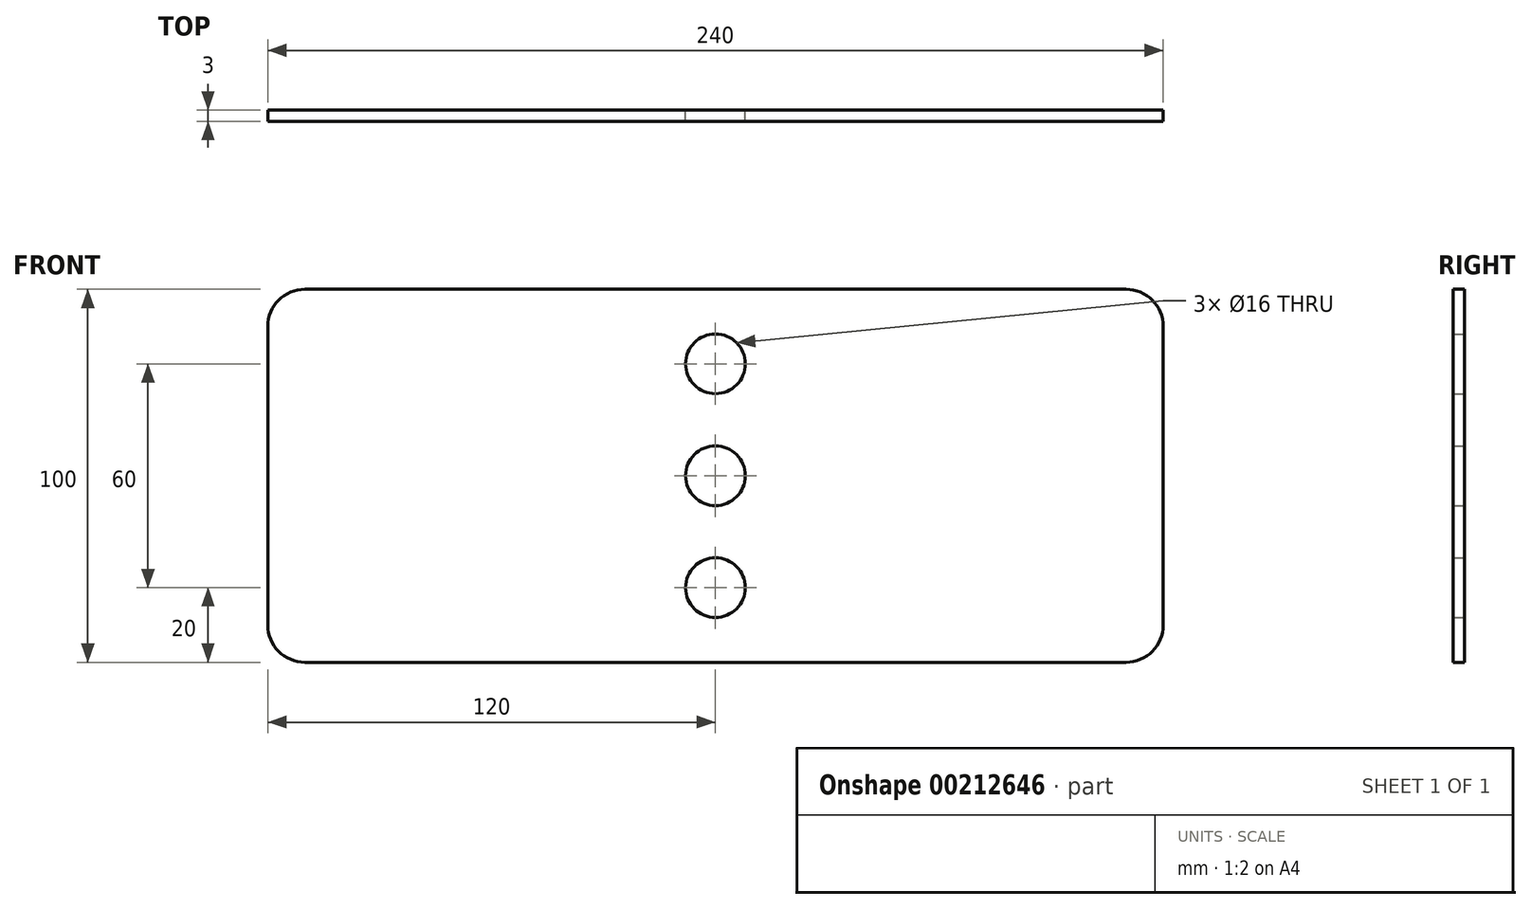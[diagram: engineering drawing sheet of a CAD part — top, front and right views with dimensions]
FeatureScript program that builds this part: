
annotation { "Feature Type Name" : "Feature", "Feature Type Description" : "" }
export const myFeature = defineFeature(function(context is Context, id is Id, definition is map)
    precondition{}
    {
        {
            var Q0;
            Q0=qCreatedBy(makeId("Front.planeOp"),FACE);
            var sketch = newSketch(context, id + "F0", { "sketchPlane" : qUnion([Q0])});
            skLineSegment(sketch, "E0.bottom", {"start": v(-120, 50) * mm, "end": v(120, 50) * mm});
            skLineSegment(sketch, "E0.top", {"start": v(-120, -50) * mm, "end": v(120, -50) * mm});
            skLineSegment(sketch, "E0.left", {"start": v(-120, 50) * mm, "end": v(-120, -50) * mm});
            skLineSegment(sketch, "E0.right", {"start": v(120, 50) * mm, "end": v(120, -50) * mm});
            skCircle(sketch, "E1", {"center": v(0, 0) * mm, "radius": 8 * mm});
            skCircle(sketch, "E2", {"center": v(0, 30) * mm, "radius": 8 * mm});
            skCircle(sketch, "E3", {"center": v(0, -30) * mm, "radius": 8 * mm});
            skSolve(sketch);
        }
        {
            var Q0;
            Q0 = qSketchRegion(id + "F0", true);
            extrude(context, id + "F1", {"entities" : qUnion([Q0]), "depth" : 3 * mm});
        }
        {
            var Q0;
            Q0=makeQuery(id+"F1.opExtrude","SWEPT_EDGE",EDGE,{"disambiguationData":[OSD([sQuery(id+"F0.wireOp",EDGE,"E0.bottom"),sQuery(id+"F0.wireOp",EDGE,"E0.left")])]});
            var Q1;
            Q1=makeQuery(id+"F1.opExtrude","SWEPT_EDGE",EDGE,{"disambiguationData":[OSD([sQuery(id+"F0.wireOp",EDGE,"E0.top"),sQuery(id+"F0.wireOp",EDGE,"E0.left")])]});
            var Q2;
            Q2=makeQuery(id+"F1.opExtrude","SWEPT_EDGE",EDGE,{"disambiguationData":[OSD([sQuery(id+"F0.wireOp",EDGE,"E0.bottom"),sQuery(id+"F0.wireOp",EDGE,"E0.right")])]});
            var Q3;
            Q3=makeQuery(id+"F1.opExtrude","SWEPT_EDGE",EDGE,{"disambiguationData":[OSD([sQuery(id+"F0.wireOp",EDGE,"E0.top"),sQuery(id+"F0.wireOp",EDGE,"E0.right")])]});
            fillet(context, id + "F2", {"entities" : qUnion([Q0, Q1, Q2, Q3]), "radius" : 10 * mm, "tangentPropagation" : true, "allowEdgeOverflow" : false});
        }
    });
